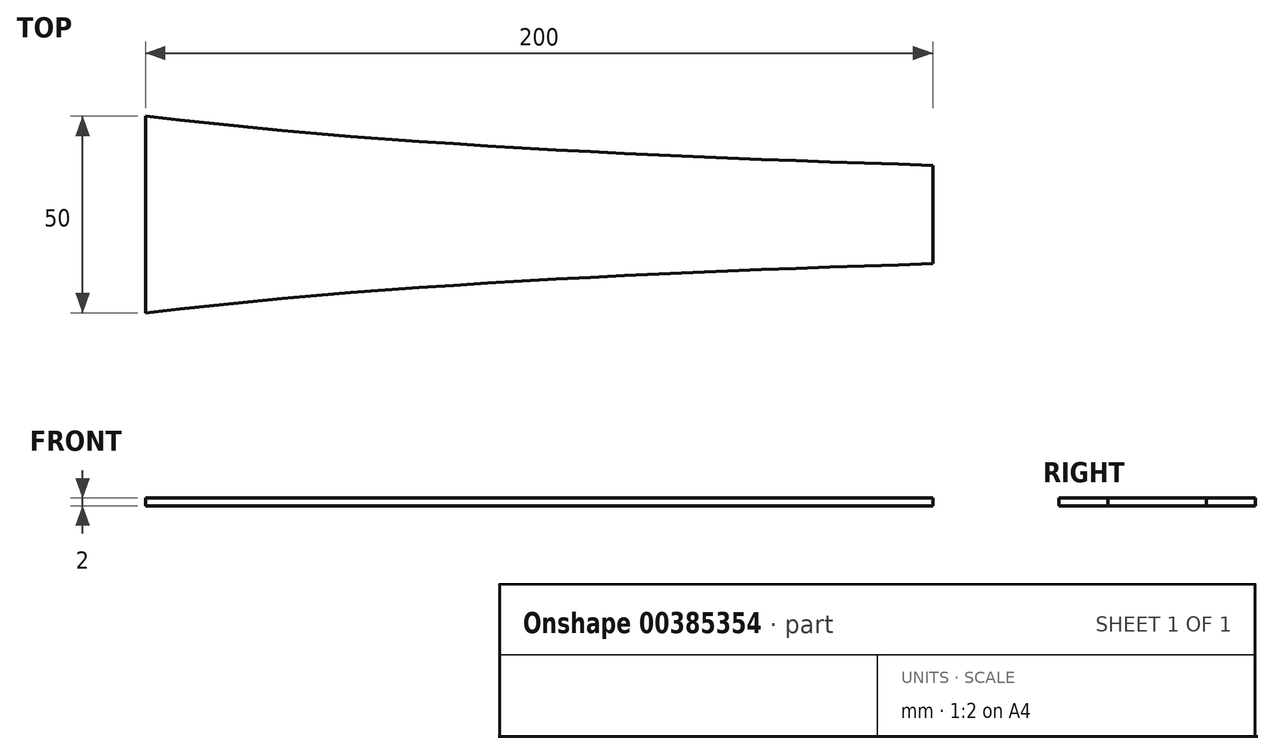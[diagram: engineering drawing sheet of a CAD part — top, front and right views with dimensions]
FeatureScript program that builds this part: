
annotation { "Feature Type Name" : "Feature", "Feature Type Description" : "" }
export const myFeature = defineFeature(function(context is Context, id is Id, definition is map)
    precondition{}
    {
        {
            var Q0;
            Q0=qCreatedBy(makeId("Top.planeOp"),FACE);
            var sketch = newSketch(context, id + "F0", { "sketchPlane" : qUnion([Q0])});
            skLineSegment(sketch, "E0", {"start": v(0, 25) * mm, "end": v(0, -25) * mm});
            skPoint(sketch, "E1", {"position": v(0, 0) * mm});
            skLineSegment(sketch, "E2", {"start": v(200, 12.5) * mm, "end": v(200, -12.5) * mm});
            skPoint(sketch, "E3", {"position": v(200, 0) * mm});
            skLineSegment(sketch, "E4", {"start": v(0, 0) * mm, "end": v(200, 0) * mm, "construction": true});
            skPoint(sketch, "E5", {"position": v(20, 22.83) * mm});
            skPoint(sketch, "E6", {"position": v(40, 20.83) * mm});
            skPoint(sketch, "E7", {"position": v(60, 19.23) * mm});
            skPoint(sketch, "E8", {"position": v(80, 17.86) * mm});
            skPoint(sketch, "E9", {"position": v(100, 16.67) * mm});
            skPoint(sketch, "E10", {"position": v(120, 15.62) * mm});
            skPoint(sketch, "E11", {"position": v(140, 14.7) * mm});
            skPoint(sketch, "E12", {"position": v(160, 13.89) * mm});
            skPoint(sketch, "E13", {"position": v(180, 13.16) * mm});
            skFitSpline(sketch, "E14", {"points": [v(0, 25) * mm, v(20, 22.83) * mm, v(40, 20.83) * mm, v(60, 19.23) * mm, v(80, 17.86) * mm, v(100, 16.67) * mm, v(120, 15.62) * mm, v(140, 14.7) * mm, v(160, 13.89) * mm, v(180, 13.16) * mm, v(200, 12.5) * mm], "startDerivative": vector(199.63, -21.87) * mm, "endDerivative": vector(200.17, -6.47) * mm});
            skFitSpline(sketch, "E15.MirrorCS", {"points": [v(0, -25) * mm, v(20, -22.83) * mm, v(40, -20.83) * mm, v(60, -19.23) * mm, v(80, -17.86) * mm, v(100, -16.67) * mm, v(120, -15.62) * mm, v(140, -14.7) * mm, v(160, -13.89) * mm, v(180, -13.16) * mm, v(200, -12.5) * mm], "startDerivative": vector(199.63, 21.87) * mm, "endDerivative": vector(200.17, 6.47) * mm});
            skSolve(sketch);
        }
        {
            var Q0;
            Q0 = qSketchRegion(id + "F0", true);
            extrude(context, id + "F1", {"entities" : qUnion([Q0]), "depth" : 2 * mm});
        }
    });
